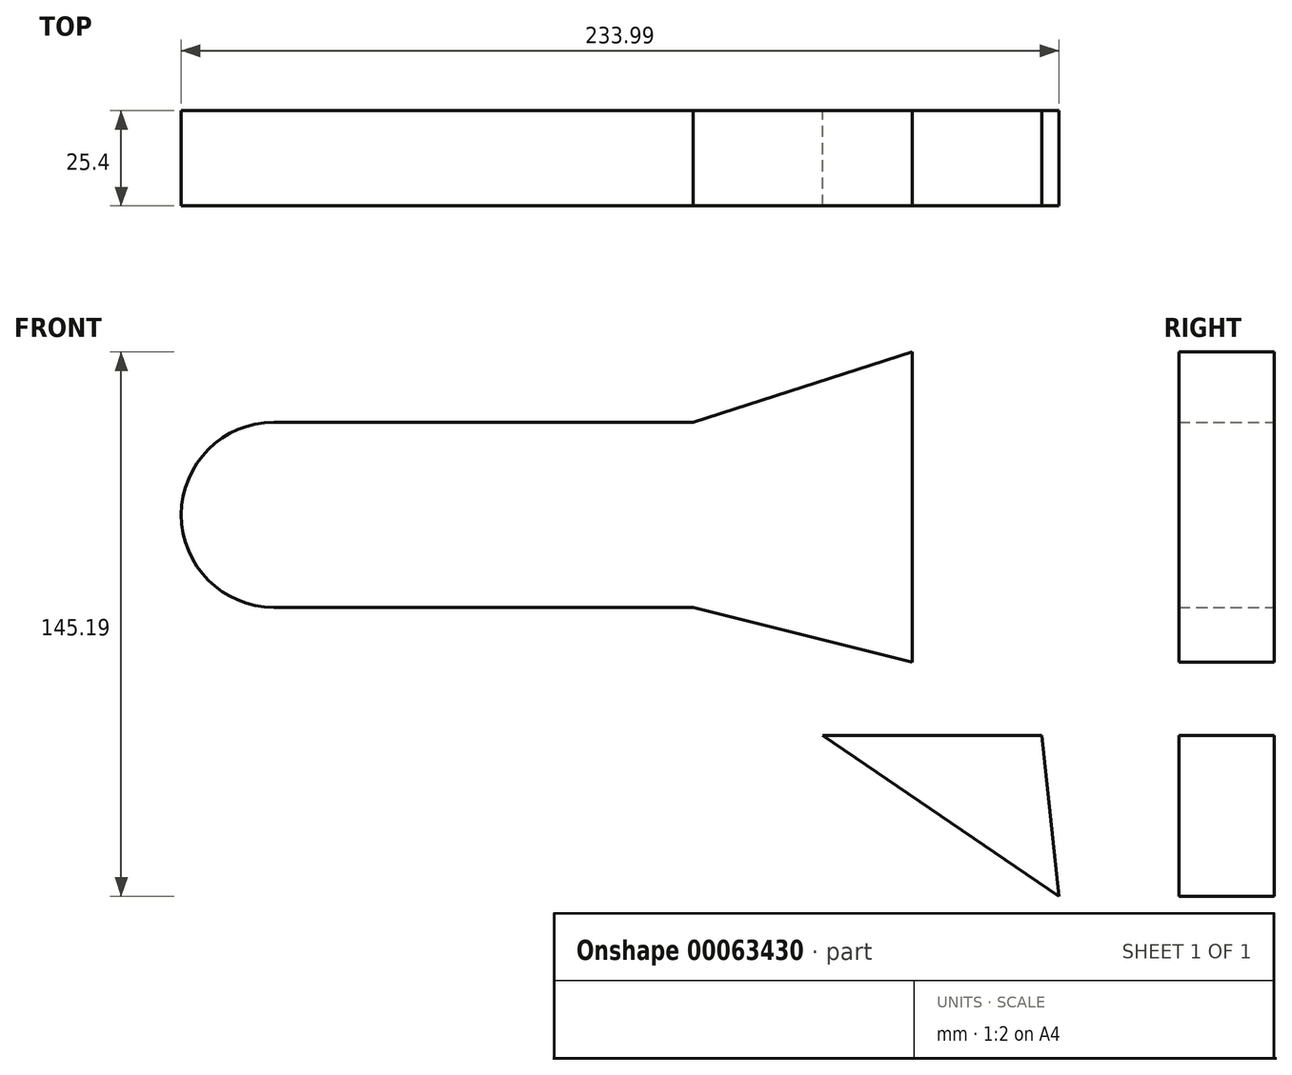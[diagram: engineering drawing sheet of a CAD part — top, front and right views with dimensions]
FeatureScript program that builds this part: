
annotation { "Feature Type Name" : "Feature", "Feature Type Description" : "" }
export const myFeature = defineFeature(function(context is Context, id is Id, definition is map)
    precondition{}
    {
        {
            var Q0;
            Q0=qCreatedBy(makeId("Front.planeOp"),FACE);
            var sketch = newSketch(context, id + "F0", { "sketchPlane" : qUnion([Q0])});
            skLineSegment(sketch, "E0.bottom", {"start": v(-192.02, 52.13) * mm, "end": v(-80.25, 52.13) * mm});
            skLineSegment(sketch, "E0.top", {"start": v(-192.02, 2.76) * mm, "end": v(-80.25, 2.76) * mm});
            skLineSegment(sketch, "E0.left", {"start": v(-192.02, 52.13) * mm, "end": v(-192.02, 2.76) * mm});
            skLineSegment(sketch, "E0.right", {"start": v(-80.25, 52.13) * mm, "end": v(-80.25, 2.76) * mm});
            skArc(sketch, "E1", {"start": v(-192.02, 52.13) * mm, "mid": v(-216.7, 27.45) * mm, "end": v(-192.02, 2.76) * mm});
            skLineSegment(sketch, "E2", {"start": v(-80.25, 52.13) * mm, "end": v(-21.82, 70.87) * mm});
            skLineSegment(sketch, "E3", {"start": v(-80.25, 2.76) * mm, "end": v(-21.82, -11.92) * mm});
            skLineSegment(sketch, "E4", {"start": v(-21.82, 70.87) * mm, "end": v(-21.82, -11.92) * mm});
            skSolve(sketch);
        }
        {
            var Q0;
            Q0 = qSketchRegion(id + "F0", true);
            extrude(context, id + "F1", {"entities" : qUnion([Q0]), "depth" : 25.4 * mm});
        }
        {
            var Q0;
            Q0 = qSketchRegion(id + "F0", true);
            extrude(context, id + "F2", {"entities" : qUnion([Q0]), "operationType" : NewBodyOperationType.ADD, "depth" : 25.4 * mm});
        }
        {
            var Q0;
            Q0=qCreatedBy(makeId("Front.planeOp"),FACE);
            var sketch = newSketch(context, id + "F3", { "sketchPlane" : qUnion([Q0])});
            skLineSegment(sketch, "E5", {"start": v(-45.67, -31.37) * mm, "end": v(17.28, -74.32) * mm});
            skLineSegment(sketch, "E6", {"start": v(-45.67, -31.37) * mm, "end": v(12.75, -31.37) * mm});
            skLineSegment(sketch, "E7", {"start": v(12.75, -31.37) * mm, "end": v(17.28, -74.32) * mm});
            skLineSegment(sketch, "E8", {"start": v(0.64, 63.02) * mm, "end": v(63.42, 63.02) * mm});
            skLineSegment(sketch, "E9", {"start": v(63.42, 63.02) * mm, "end": v(63.42, 19.84) * mm});
            skLineSegment(sketch, "E10", {"start": v(63.42, 19.84) * mm, "end": v(0.64, 63.02) * mm});
            skSolve(sketch);
        }
        {
            var Q0;
            Q0=makeQuery(id+"F3.imprint","IMPRINT",FACE,{"disambiguationData":[TD([[makeQuery(id+"F3.imprint","IMPRINT",EDGE,{"derivedFrom":sQuery(id+"F3.wireOp",EDGE,"E5")}),1.0]])]});
            extrude(context, id + "F4", {"entities" : qUnion([Q0]), "depth" : 25.4 * mm});
        }
        {
            var Q0;
            Q0=sQuery(id+"F3.wireOp",EDGE,"E8");
            var Q1;
            Q1=sQuery(id+"F3.wireOp",EDGE,"E9");
            var Q2;
            Q2=sQuery(id+"F3.wireOp",EDGE,"E10");
            extrude(context, id + "F5", {"bodyType" : ToolBodyType.SURFACE, "surfaceEntities" : qUnion([Q0, Q1, Q2]), "depth" : 25.4 * mm});
        }
    });
